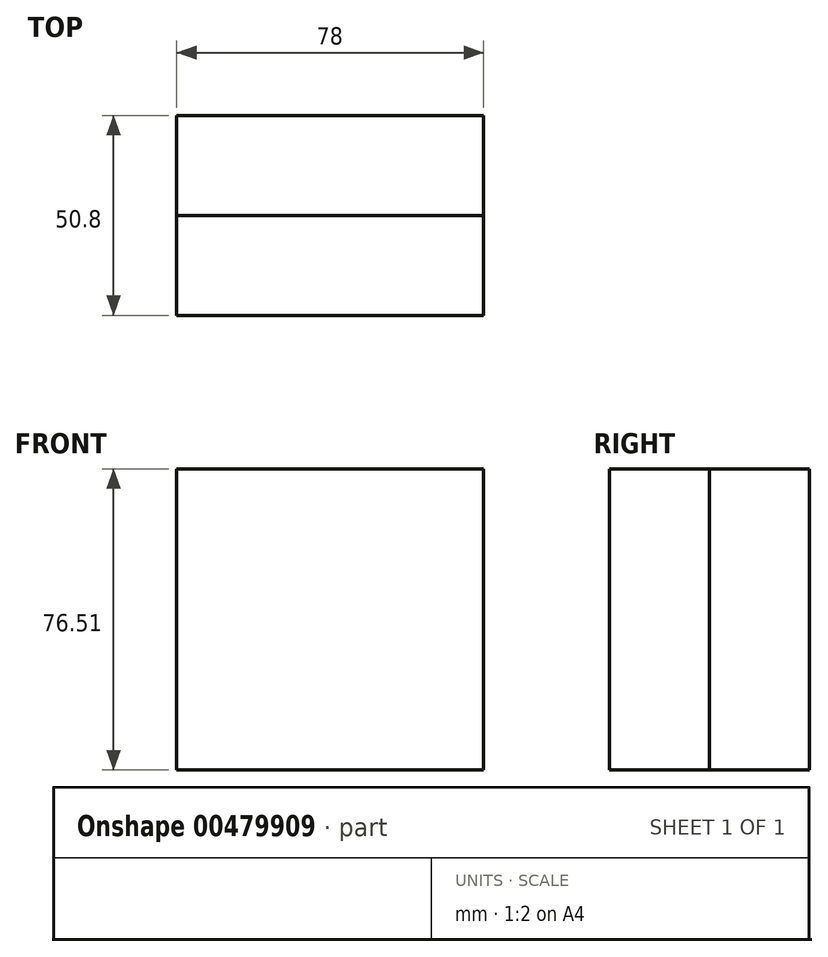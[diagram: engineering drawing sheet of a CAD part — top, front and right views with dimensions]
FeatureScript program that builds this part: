
annotation { "Feature Type Name" : "Feature", "Feature Type Description" : "" }
export const myFeature = defineFeature(function(context is Context, id is Id, definition is map)
    precondition{}
    {
        {
            var Q0;
            Q0=qCreatedBy(makeId("Front.planeOp"),FACE);
            var sketch = newSketch(context, id + "F0", { "sketchPlane" : qUnion([Q0])});
            skLineSegment(sketch, "E0.bottom", {"start": v(-169.9, 25.22) * mm, "end": v(-91.9, 25.22) * mm});
            skLineSegment(sketch, "E0.top", {"start": v(-169.9, -51.29) * mm, "end": v(-91.9, -51.29) * mm});
            skLineSegment(sketch, "E0.left", {"start": v(-169.9, 25.22) * mm, "end": v(-169.9, -51.29) * mm});
            skLineSegment(sketch, "E0.right", {"start": v(-91.9, 25.22) * mm, "end": v(-91.9, -51.29) * mm});
            skSolve(sketch);
        }
        {
            var Q0;
            Q0 = qSketchRegion(id + "F0", true);
            extrude(context, id + "F1", {"entities" : qUnion([Q0]), "depth" : 25.4 * mm});
        }
        {
            var Q0;
            Q0=makeQuery(id+"F1.opExtrude","CAP_FACE",FACE,{"disambiguationData":[OSD([sQuery(id+"F0.wireOp",EDGE,"E0.bottom"),sQuery(id+"F0.wireOp",EDGE,"E0.top"),sQuery(id+"F0.wireOp",EDGE,"E0.left"),sQuery(id+"F0.wireOp",EDGE,"E0.right")])],"isStart":false});
            extrude(context, id + "F2", {"entities" : qUnion([Q0]), "depth" : 25.4 * mm});
        }
    });
